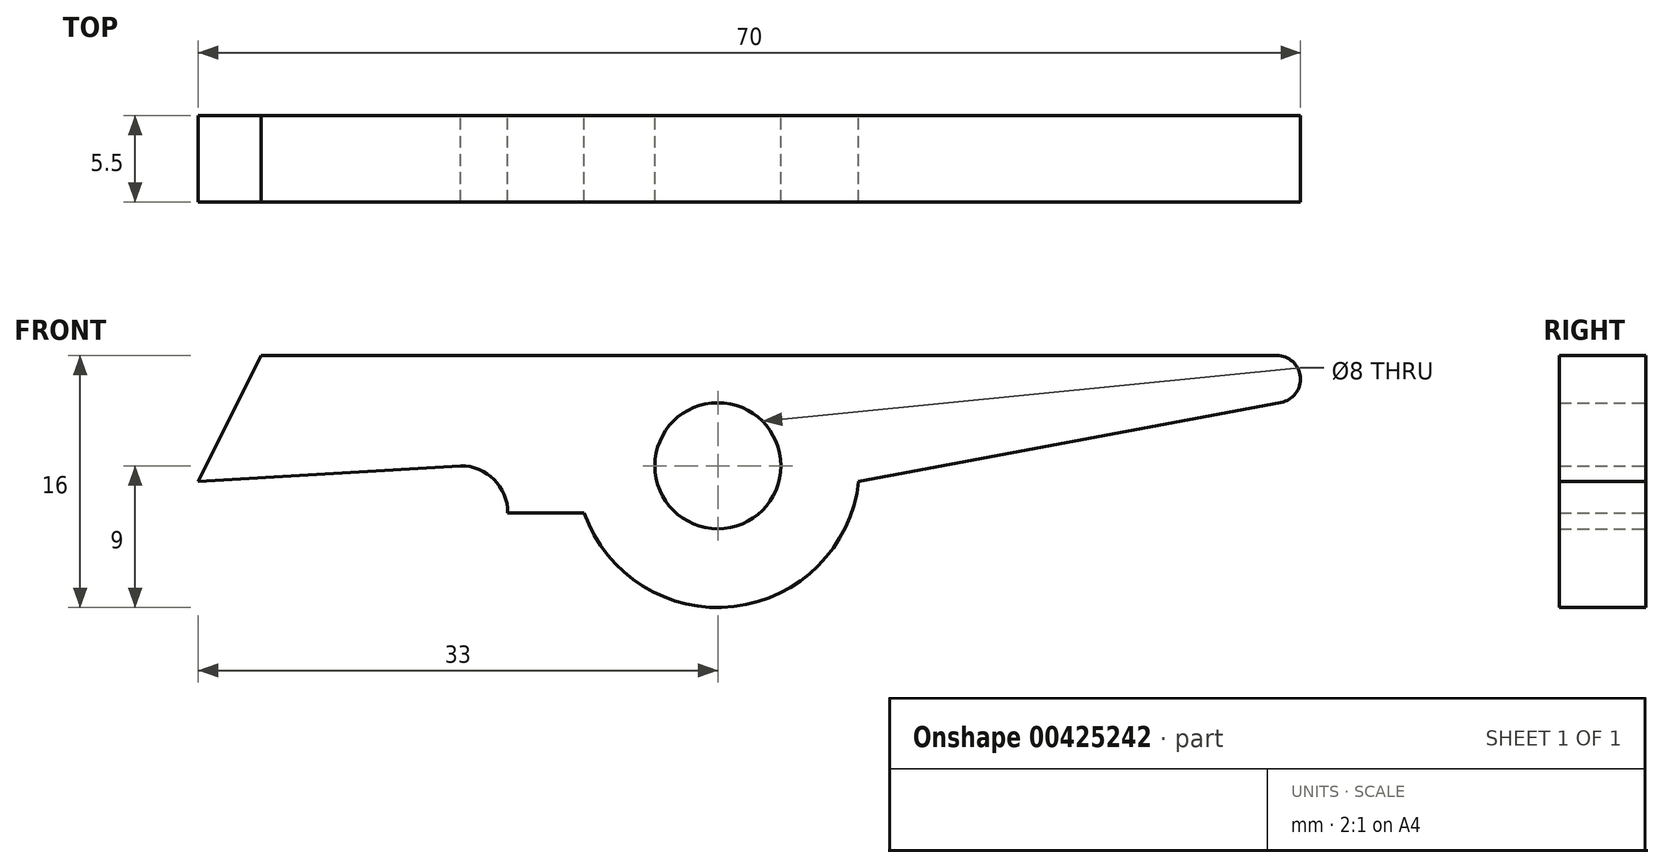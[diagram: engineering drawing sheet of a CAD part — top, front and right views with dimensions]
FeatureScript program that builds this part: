
annotation { "Feature Type Name" : "Feature", "Feature Type Description" : "" }
export const myFeature = defineFeature(function(context is Context, id is Id, definition is map)
    precondition{}
    {
        {
            var Q0;
            Q0=qCreatedBy(makeId("Front.planeOp"),FACE);
            var sketch = newSketch(context, id + "F0", { "sketchPlane" : qUnion([Q0])});
            skCircle(sketch, "E0", {"center": v(0, 0) * mm, "radius": 4 * mm});
            skArc(sketch, "E1", {"start": v(-8.49, -3) * mm, "mid": v(1.03, -8.94) * mm, "end": v(8.94, -1) * mm});
            skLineSegment(sketch, "E2", {"start": v(-8.49, -3) * mm, "end": v(-13.34, -3) * mm});
            skLineSegment(sketch, "E3", {"start": v(8.94, -1) * mm, "end": v(35.78, 4.03) * mm});
            skArc(sketch, "E4", {"start": v(35.5, 7) * mm, "mid": v(37, 5.64) * mm, "end": v(35.78, 4.03) * mm});
            skLineSegment(sketch, "E5", {"start": v(35.5, 7) * mm, "end": v(-29, 7) * mm});
            skArc(sketch, "E6", {"start": v(-13.34, -3) * mm, "mid": v(-14.22, -0.88) * mm, "end": v(-16.34, 0) * mm});
            skLineSegment(sketch, "E7", {"start": v(-33, -1) * mm, "end": v(-29, 7) * mm});
            skLineSegment(sketch, "E8", {"start": v(-33, -1) * mm, "end": v(-16.34, 0) * mm});
            skSolve(sketch);
        }
        {
            var Q0;
            Q0=makeQuery(id+"F0.imprint","IMPRINT",FACE,{"disambiguationData":[TD([[makeQuery(id+"F0.imprint","IMPRINT",EDGE,{"derivedFrom":sQuery(id+"F0.wireOp",EDGE,"E0")}),-1.0]])]});
            extrude(context, id + "F1", {"entities" : qUnion([Q0]), "endBound" : BoundingType.SYMMETRIC, "depth" : 5.5 * mm});
        }
    });
